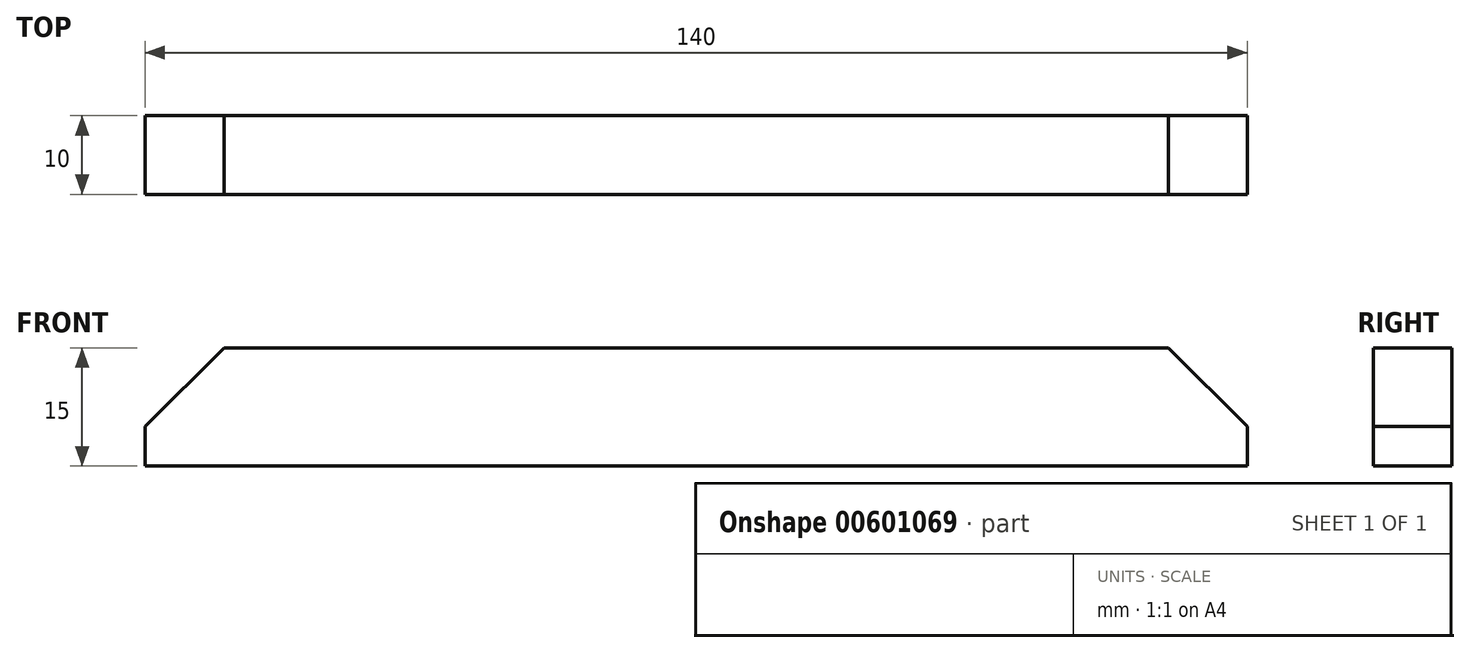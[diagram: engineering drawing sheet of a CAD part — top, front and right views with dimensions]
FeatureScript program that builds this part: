
annotation { "Feature Type Name" : "Feature", "Feature Type Description" : "" }
export const myFeature = defineFeature(function(context is Context, id is Id, definition is map)
    precondition{}
    {
        {
            var Q0;
            Q0=qCreatedBy(makeId("Front.planeOp"),FACE);
            var sketch = newSketch(context, id + "F0", { "sketchPlane" : qUnion([Q0])});
            skLineSegment(sketch, "E0.bottom", {"start": v(-54.3, 2.72) * mm, "end": v(65.7, 2.72) * mm});
            skLineSegment(sketch, "E0.top", {"start": v(-54.3, -12.28) * mm, "end": v(65.7, -12.28) * mm});
            skLineSegment(sketch, "E1", {"start": v(-64.3, -7.28) * mm, "end": v(-64.3, -12.28) * mm});
            skLineSegment(sketch, "E2", {"start": v(-64.3, -12.28) * mm, "end": v(-54.3, -12.28) * mm});
            skLineSegment(sketch, "E3", {"start": v(65.7, 2.72) * mm, "end": v(75.7, -7.28) * mm});
            skLineSegment(sketch, "E4", {"start": v(75.7, -7.28) * mm, "end": v(75.7, -12.28) * mm});
            skLineSegment(sketch, "E5", {"start": v(75.7, -12.28) * mm, "end": v(65.7, -12.28) * mm});
            skLineSegment(sketch, "E6", {"start": v(65.7, 2.72) * mm, "end": v(65.7, -12.28) * mm});
            skLineSegment(sketch, "E7", {"start": v(-54.3, -12.28) * mm, "end": v(-54.3, 2.72) * mm});
            skLineSegment(sketch, "E8", {"start": v(-54.3, 2.72) * mm, "end": v(-64.3, -7.28) * mm});
            skSolve(sketch);
        }
        {
            var Q0;
            Q0 = qSketchRegion(id + "F0", true);
            extrude(context, id + "F1", {"entities" : qUnion([Q0]), "depth" : 10 * mm, "offsetDistance" : 25.4 * mm});
        }
    });
